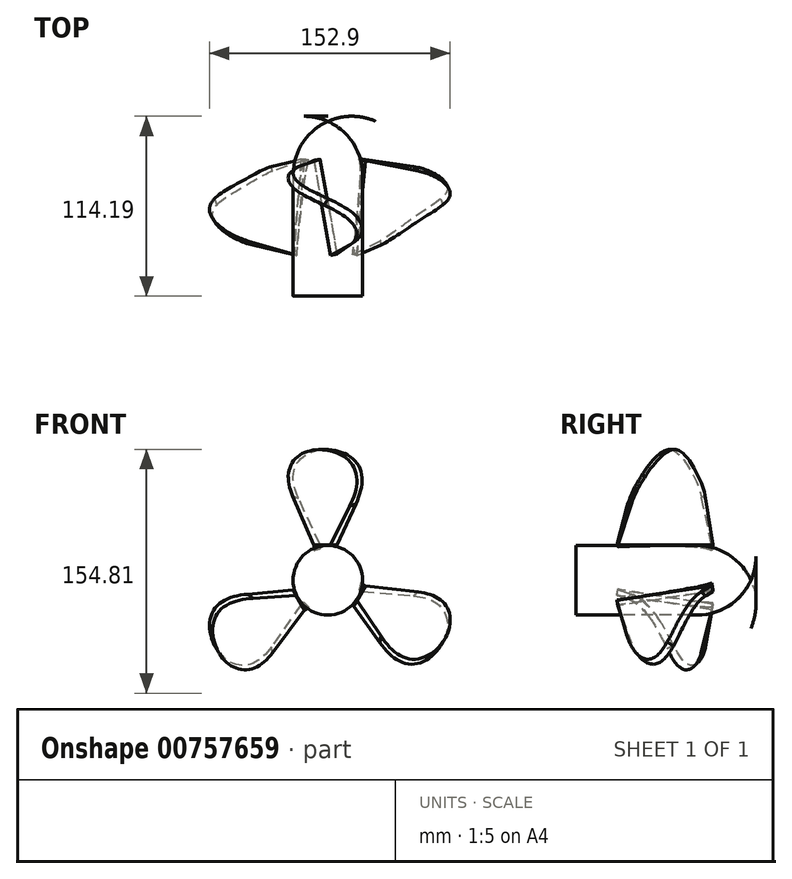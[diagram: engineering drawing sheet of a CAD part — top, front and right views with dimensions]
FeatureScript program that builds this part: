
annotation { "Feature Type Name" : "Feature", "Feature Type Description" : "" }
export const myFeature = defineFeature(function(context is Context, id is Id, definition is map)
    precondition{}
    {
        {
            var Q0;
            Q0=qCreatedBy(makeId("Right.planeOp"),FACE);
            var sketch = newSketch(context, id + "F0", { "sketchPlane" : qUnion([Q0])});
            skLineSegment(sketch, "E0", {"start": v(-50.75, 0) * mm, "end": v(-50.75, 22.06) * mm});
            skLineSegment(sketch, "E1", {"start": v(-50.75, 22.06) * mm, "end": v(0, 22.06) * mm});
            skLineSegment(sketch, "E2", {"start": v(-50.75, 0) * mm, "end": v(34.03, 0) * mm});
            skArc(sketch, "E3", {"start": v(34.03, 0) * mm, "mid": v(20.28, 16.06) * mm, "end": v(0, 22.06) * mm});
            skSolve(sketch);
        }
        {
            var Q0;
            Q0=makeQuery(id+"F0.imprint","IMPRINT",FACE,{"disambiguationData":[TD([[makeQuery(id+"F0.imprint","IMPRINT",EDGE,{"derivedFrom":sQuery(id+"F0.wireOp",EDGE,"E0")}),-1.0]])]});
            var Q1;
            Q1=sQuery(id+"F0.wireOp",EDGE,"E2");
            revolve(context, id + "F1", {"entities" : qUnion([Q0]), "axis" : qUnion([Q1]), "revolveType" : RevolveType.FULL});
        }
        {
            var Q0;
            Q0=qCreatedBy(makeId("Top.planeOp"),FACE);
            var sketch = newSketch(context, id + "F2", { "sketchPlane" : qUnion([Q0])});
            skLineSegment(sketch, "E4.bottom", {"start": v(-8.85, 9.23) * mm, "end": v(-4.85, 9.93) * mm});
            skLineSegment(sketch, "E4.top", {"start": v(1.78, -51.05) * mm, "end": v(5.78, -50.34) * mm});
            skLineSegment(sketch, "E4.left", {"start": v(-8.85, 9.23) * mm, "end": v(1.78, -51.05) * mm});
            skLineSegment(sketch, "E4.right", {"start": v(-4.85, 9.93) * mm, "end": v(5.78, -50.34) * mm});
            skSolve(sketch);
        }
        {
            var Q0;
            Q0=qCreatedBy(makeId("Top.planeOp"),FACE);
            cPlane(context, id + "F3", {"entities" : qUnion([Q0]), "cplaneType" : CPlaneType.OFFSET, "offset" : 83.06 * mm, "width" : 152.4 * mm, "height" : 152.4 * mm});
        }
        {
            var Q0;
            Q0=qCreatedBy(id+"F3.planeOp",FACE);
            var sketch = newSketch(context, id + "F4", { "sketchPlane" : qUnion([Q0])});
            skLineSegment(sketch, "E5.bottom", {"start": v(-35.01, -3.9) * mm, "end": v(-33, 0.4) * mm});
            skLineSegment(sketch, "E5.top", {"start": v(31.59, -34.96) * mm, "end": v(33.6, -30.66) * mm});
            skLineSegment(sketch, "E5.left", {"start": v(-35.01, -3.9) * mm, "end": v(31.59, -34.96) * mm});
            skLineSegment(sketch, "E5.right", {"start": v(-33, 0.4) * mm, "end": v(33.6, -30.66) * mm});
            skSolve(sketch);
        }
        {
            var Q0;
            Q0=makeQuery(id+"F1.opRevolve","SWEPT_FACE",FACE,{"disambiguationData":[OSD([sQuery(id+"F0.wireOp",EDGE,"E0")])]});
            extrude(context, id + "F5", {"entities" : qUnion([Q0]), "operationType" : NewBodyOperationType.ADD, "depth" : 40.64 * mm, "offsetDistance" : 25.4 * mm});
        }
        {
            var Q0;
            Q0=qSketchRegion(id+"F2",true);
            extrude(context, id + "F6", {"entities" : qUnion([Q0]), "operationType" : NewBodyOperationType.ADD, "depth" : 22.35 * mm});
        }
        {
            var Q1;
            Q1=makeQuery(id+"F6.opExtrude","CAP_FACE",FACE,{"disambiguationData":[OSD([sQuery(id+"F2.wireOp",EDGE,"E4.bottom"),sQuery(id+"F2.wireOp",EDGE,"E4.top"),sQuery(id+"F2.wireOp",EDGE,"E4.left"),sQuery(id+"F2.wireOp",EDGE,"E4.right")])],"isStart":false});
            var Q2;
            Q2=makeQuery(id+"F4.imprint","IMPRINT",FACE,{"disambiguationData":[TD([[makeQuery(id+"F4.imprint","IMPRINT",EDGE,{"derivedFrom":sQuery(id+"F4.wireOp",EDGE,"E5.bottom")}),-1.0]])]});
            loft(context, id + "F7", {"operationType" : NewBodyOperationType.ADD, "sheetProfilesArray" : [{ "sheetProfileEntities" : qUnion([Q1]) }, { "sheetProfileEntities" : qUnion([Q2]) }]});
        }
        {
            var Q0;
            Q0=makeQuery(id+"F7.opLoft","MID_CAP_EDGE",EDGE,{"disambiguationData":[OSD([sQuery(id+"F4.wireOp",EDGE,"E5.top"),sQuery(id+"F4.wireOp",EDGE,"E5.left"),sQuery(id+"F4.wireOp",EDGE,"E5.right")])],"capPos":1.0});
            fillet(context, id + "F8", {"entities" : qUnion([Q0]), "radius" : 34.31 * mm, "tangentPropagation" : true, "allowEdgeOverflow" : false});
        }
        {
            var Q0;
            Q0=makeQuery(id+"F7.opLoft","MID_CAP_EDGE",EDGE,{"disambiguationData":[OSD([sQuery(id+"F4.wireOp",EDGE,"E5.bottom"),sQuery(id+"F4.wireOp",EDGE,"E5.left"),sQuery(id+"F4.wireOp",EDGE,"E5.right")])],"capPos":1.0});
            fillet(context, id + "F9", {"entities" : qUnion([Q0]), "radius" : 26.37 * mm, "tangentPropagation" : true, "allowEdgeOverflow" : false});
        }
        {
            var Q0;
            Q0=makeQuery(id+"F5.opExtrude","CAP_FACE",FACE,{"disambiguationData":[OSD([sQuery(id+"F0.wireOp",EDGE,"E0")])],"isStart":false});
            extrude(context, id + "F10", {"entities" : qUnion([Q0]), "operationType" : NewBodyOperationType.REMOVE, "oppositeDirection" : true, "depth" : 14.48 * mm});
        }
        {
            var Q0;
            Q0=makeQuery(id+"F1.opRevolve","SWEPT_BODY",BODY,{"disambiguationData":[OSD([sQuery(id+"F0.wireOp",EDGE,"E0"),sQuery(id+"F0.wireOp",EDGE,"E1"),sQuery(id+"F0.wireOp",EDGE,"E2"),sQuery(id+"F0.wireOp",EDGE,"E3")])]});
            var Q1;
            Q1=sQuery(id+"F0.wireOp",EDGE,"E2");
            circularPattern(context, id + "F11", {"entities" : qUnion([Q0]), "axis" : qUnion([Q1]), "angle" : 360 * degree, "instanceCount" : 3, "equalSpace" : true});
        }
        {
            var Q0;
            {var subQ0=sQuery(id+"F2.wireOp",EDGE,"E4.bottom");Q0=makeQuery(id+"F7.boolean.opBoolean","MERGE",EDGE,{"derivedFrom":[makeQuery(id+"F6.opExtrude","CAP_EDGE",EDGE,{"disambiguationData":[OSD([subQ0])],"isStart":false}),makeQuery(id+"F7.opLoft","MID_CAP_EDGE",EDGE,{"disambiguationData":[OSD([subQ0,sQuery(id+"F2.wireOp",EDGE,"E4.left"),sQuery(id+"F2.wireOp",EDGE,"E4.right")])],"capPos":0.0})]});}
            fillet(context, id + "F12", {"entities" : qUnion([Q0]), "radius" : 7.15 * mm, "tangentPropagation" : true, "allowEdgeOverflow" : false});
        }
    });
